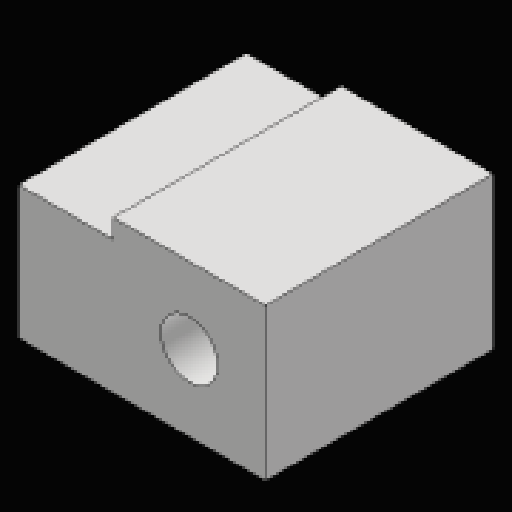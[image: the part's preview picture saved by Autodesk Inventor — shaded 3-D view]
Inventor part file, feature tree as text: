
AUTODESK INVENTOR PART (.ipt)
format: ipt  version: 2023.2 (Build 272271030, 271C)  size: 99,840 bytes
history: native  units: mm
features: extrude x2, sketch x2, projected_geometry x1
ambient origin geometry x8: Origin, YZ Plane, XZ Plane, XY Plane, X Axis, Y Axis, Z Axis, Center Point
bodies: Solid1 (feature_tree)
feature tree (5):
  extrude  "Extrusion1"  Depth=8.0mm
  extrude  "Extrusion2"  Depth=7.0mm
  sketch  "Sketch1"  dims[d0=8.0mm d1=8.0mm]
  sketch  "Sketch2"  dims[d2=12.0mm d3=0.0mm d4=4.0mm d6=0.0mm d7=0.0mm d8=8.0mm d9=7.0mm]
  projected_geometry  "Projected Loop1"
